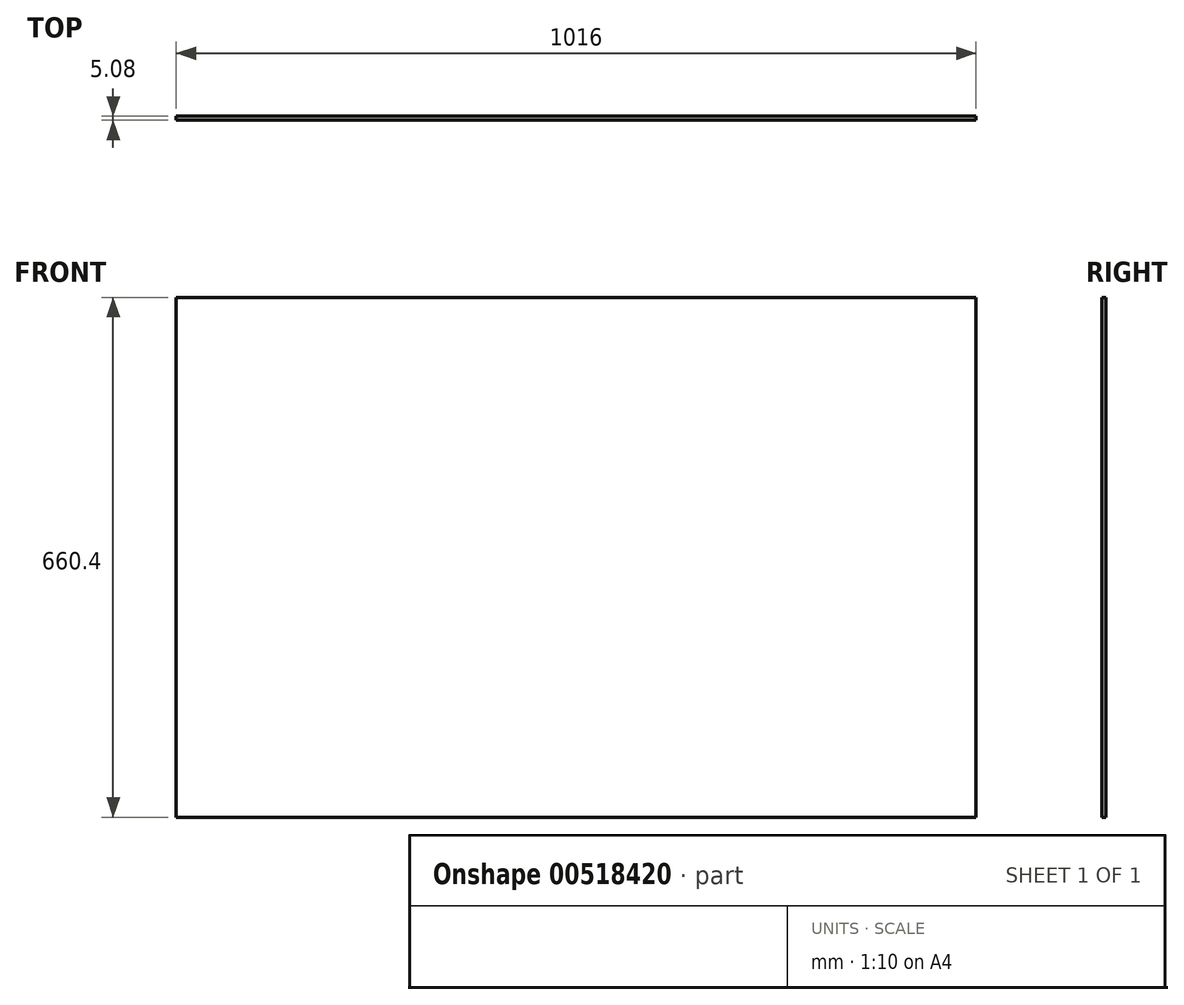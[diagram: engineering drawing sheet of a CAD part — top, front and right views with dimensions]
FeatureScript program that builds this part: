
annotation { "Feature Type Name" : "Feature", "Feature Type Description" : "" }
export const myFeature = defineFeature(function(context is Context, id is Id, definition is map)
    precondition{}
    {
        {
            var Q0;
            Q0=qCreatedBy(makeId("Front.planeOp"),FACE);
            var sketch = newSketch(context, id + "F0", { "sketchPlane" : qUnion([Q0])});
            skLineSegment(sketch, "E0.bottom", {"start": v(-508, 330.2) * mm, "end": v(508, 330.2) * mm});
            skLineSegment(sketch, "E0.top", {"start": v(-508, -330.2) * mm, "end": v(508, -330.2) * mm});
            skLineSegment(sketch, "E0.left", {"start": v(-508, 330.2) * mm, "end": v(-508, -330.2) * mm});
            skLineSegment(sketch, "E0.right", {"start": v(508, 330.2) * mm, "end": v(508, -330.2) * mm});
            skPoint(sketch, "E0.middle", {"position": v(0, 0) * mm});
            skSolve(sketch);
        }
        {
            var Q0;
            Q0 = qSketchRegion(id + "F0", true);
            extrude(context, id + "F1", {"entities" : qUnion([Q0]), "depth" : 5.08 * mm, "offsetDistance" : 25.4 * mm});
        }
    });
